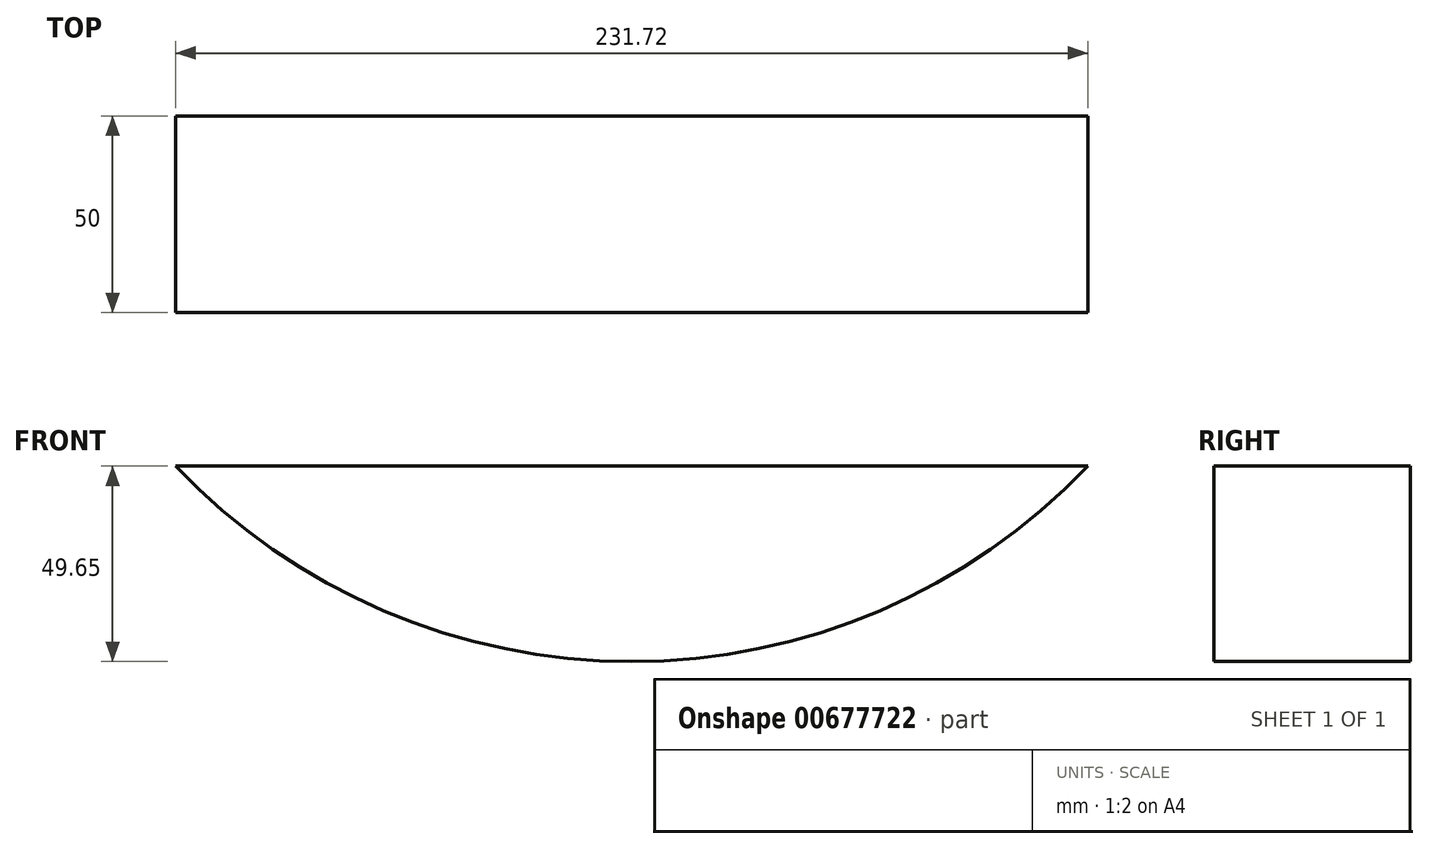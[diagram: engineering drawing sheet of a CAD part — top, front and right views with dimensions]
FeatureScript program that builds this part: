
annotation { "Feature Type Name" : "Feature", "Feature Type Description" : "" }
export const myFeature = defineFeature(function(context is Context, id is Id, definition is map)
    precondition{}
    {
        {
            var Q0;
            Q0=qCreatedBy(makeId("Front.planeOp"),FACE);
            var sketch = newSketch(context, id + "F0", { "sketchPlane" : qUnion([Q0])});
            skLineSegment(sketch, "E0", {"start": v(-99.1, 49.63) * mm, "end": v(132.63, 49.63) * mm});
            skArc(sketch, "E1", {"start": v(-99.1, 49.63) * mm, "mid": v(16.77, -0.02) * mm, "end": v(132.63, 49.63) * mm});
            skSolve(sketch);
        }
        {
            var Q0;
            Q0=makeQuery(id+"F0.imprint","IMPRINT",FACE,{"disambiguationData":[TD([[makeQuery(id+"F0.imprint","IMPRINT",EDGE,{"derivedFrom":sQuery(id+"F0.wireOp",EDGE,"E0")}),-1.0]])]});
            extrude(context, id + "F1", {"entities" : qUnion([Q0]), "endBound" : BoundingType.SYMMETRIC, "depth" : 50 * mm, "offsetDistance" : 25.4 * mm});
        }
    });
